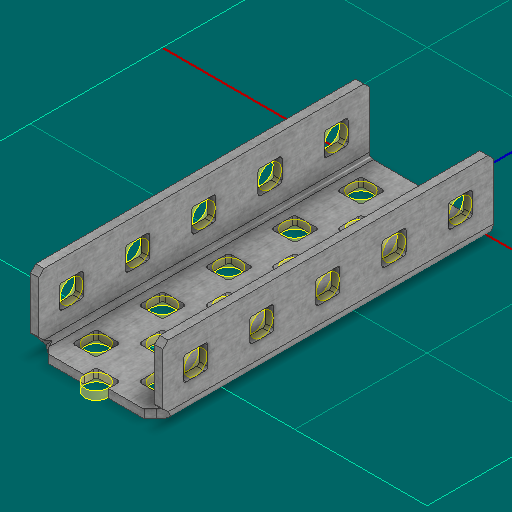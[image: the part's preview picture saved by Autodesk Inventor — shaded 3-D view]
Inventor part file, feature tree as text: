
AUTODESK INVENTOR PART (.ipt)
format: ipt  version: 2025 (Build 290162000, 162)  size: 662,016 bytes
history: native  units: in
note: dims shown in document units (in); Inventor stores cm internally (conversion verified against a paired STEP export)
features: other x56, sketch x5, sheet_metal_op x1
ambient origin geometry x8: Origin, YZ Plane, XZ Plane, XY Plane, X Axis, Y Axis, Z Axis, Center Point
bodies: Solid1 (feature_tree)
feature tree (62):
  other  "Alu C 1x2x1x5.ipt"
  other  "Solid1::Alu C 1x2x1x5.ipt"
  other  "TaggingFeature1"
  sketch  "Sketch1"  dims[d0=0.3937in]
  sketch  "Sketch2"  dims[d1=0.0625in]
  sketch  "Sketch3"
  other  "Flange Pattern Sketch"
  sketch  "Sketch9"
  sheet_metal_op  "Body Pattern Sketch"
  other  "Arc Length"
  sketch  "Sketch14"
  other  "Flange Pattern Plane"
  other  "Srf1"
  other  "Srf2"
  other  "Srf3"
  other  "Srf4"
  other  "Srf5"
  other  "Srf6"
  other  "Srf7"
  other  "Srf8"
  other  "Srf9"
  other  "Srf10"
  other  "Srf11"
  other  "Srf12"
  other  "Srf13"
  other  "Srf14"
  other  "Srf15"
  other  "Srf16"
  other  "Srf17"
  other  "Srf18"
  other  "Srf19"
  other  "Srf20"
  other  "Srf21"
  other  "Srf22"
  other  "Srf23"
  other  "Srf24"
  other  "Srf25"
  other  "Srf1::Derived"
  other  "Srf2::Derived"
  other  "Srf823::Derived"
  other  "Srf824::Derived"
  other  "Srf825::Derived"
  other  "Srf826::Derived"
  other  "Srf827::Derived"
  other  "Srf828::Derived"
  other  "Srf829::Derived"
  other  "Srf922::Derived"
  other  "Srf91::Derived"
  other  "Srf92::Derived"
  other  "Srf856::Derived"
  other  "Srf857::Derived"
  other  "Srf858::Derived"
  other  "Srf859::Derived"
  other  "Srf860::Derived"
  other  "Srf861::Derived"
  other  "Srf862::Derived"
  other  "Srf959::Derived"
  other  "Srf786::Derived"
  other  "Srf889::Derived"
  other  "Srf890::Derived"
  other  "Srf891::Derived"
  other  "Srf892::Derived"
